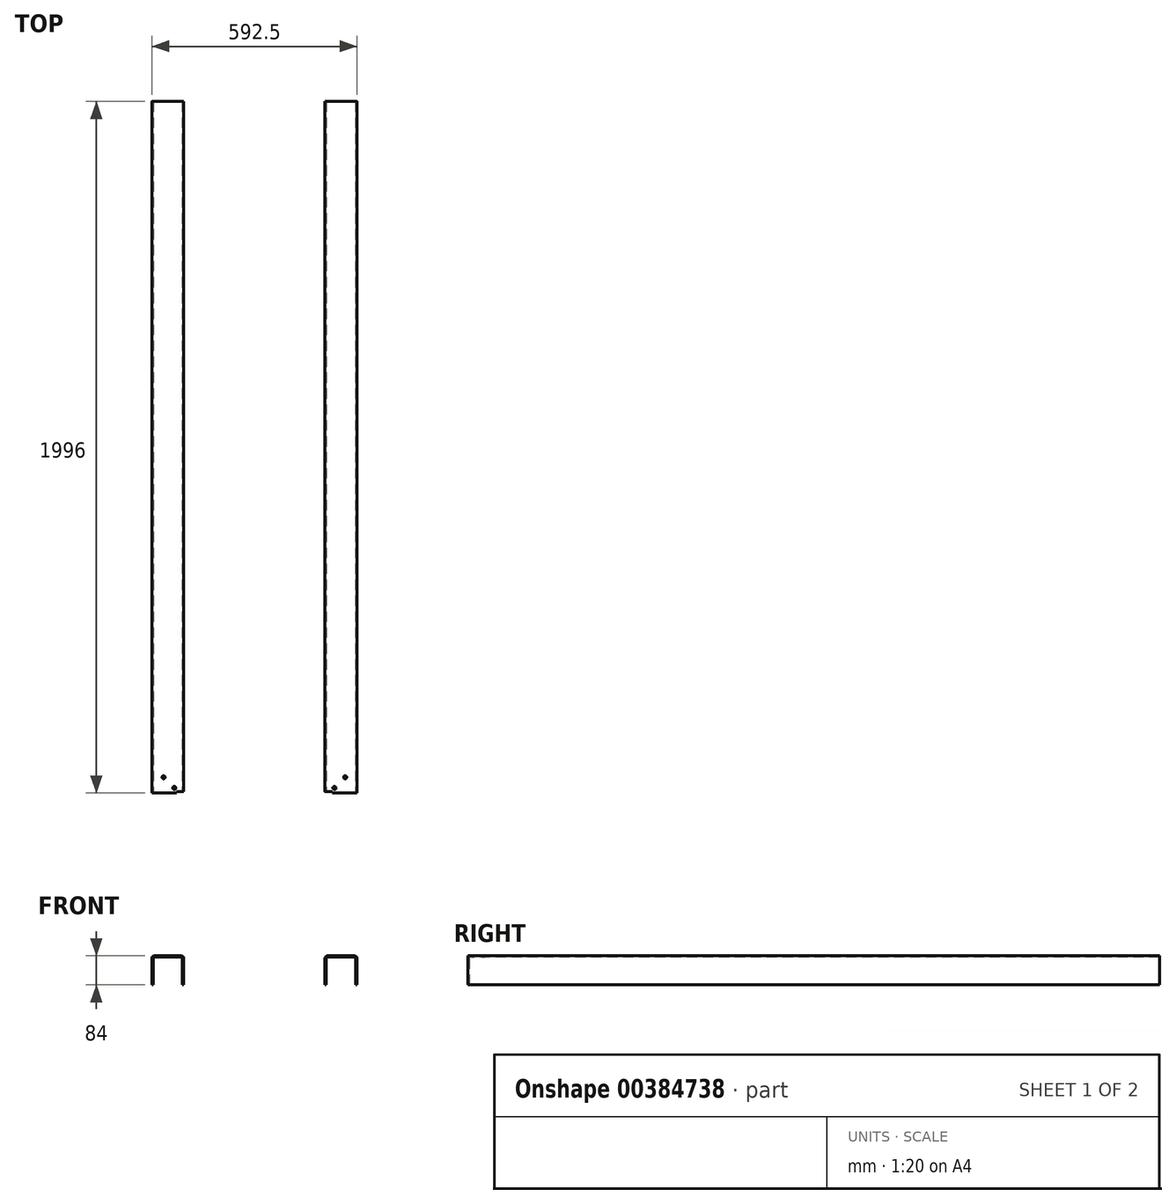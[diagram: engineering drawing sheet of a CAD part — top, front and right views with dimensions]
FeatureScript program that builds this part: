
annotation { "Feature Type Name" : "Feature", "Feature Type Description" : "" }
export const myFeature = defineFeature(function(context is Context, id is Id, definition is map)
    precondition{}
    {
        {
            var Q0;
            Q0=qCreatedBy(makeId("Front.planeOp"),FACE);
            var sketch = newSketch(context, id + "F0", { "sketchPlane" : qUnion([Q0])});
            skLineSegment(sketch, "E0.bottom", {"start": v(-46.25, -42) * mm, "end": v(-42.25, -42) * mm});
            skLineSegment(sketch, "E0.top", {"start": v(-38.25, 42) * mm, "end": v(38.25, 42) * mm});
            skLineSegment(sketch, "E0.left", {"start": v(-46.25, -42) * mm, "end": v(-46.25, 34) * mm});
            skLineSegment(sketch, "E0.right", {"start": v(46.25, -42) * mm, "end": v(46.25, 34) * mm});
            skPoint(sketch, "E0.middle", {"position": v(0, 0) * mm});
            skLineSegment(sketch, "E1", {"start": v(-42.25, -42) * mm, "end": v(-42.25, 34) * mm});
            skLineSegment(sketch, "E2", {"start": v(-38.25, 38) * mm, "end": v(38.25, 38) * mm});
            skLineSegment(sketch, "E3", {"start": v(42.25, 34) * mm, "end": v(42.25, -42) * mm});
            skLineSegment(sketch, "E4.trimOffspring", {"start": v(42.25, -42) * mm, "end": v(46.25, -42) * mm});
            skPoint(sketch, "E5.visualSharp", {"position": v(-42.25, 38) * mm});
            skArc(sketch, "E5.filletArc", {"start": v(-38.25, 38) * mm, "mid": v(-41.08, 36.83) * mm, "end": v(-42.25, 34) * mm});
            skPoint(sketch, "E6.visualSharp", {"position": v(42.25, 38) * mm});
            skArc(sketch, "E6.filletArc", {"start": v(42.25, 34) * mm, "mid": v(41.08, 36.83) * mm, "end": v(38.25, 38) * mm});
            skPoint(sketch, "E7.visualSharp", {"position": v(-46.25, 42) * mm});
            skArc(sketch, "E7.filletArc", {"start": v(-38.25, 42) * mm, "mid": v(-43.9, 39.66) * mm, "end": v(-46.25, 34) * mm});
            skPoint(sketch, "E8.visualSharp", {"position": v(46.25, 42) * mm});
            skArc(sketch, "E8.filletArc", {"start": v(46.25, 34) * mm, "mid": v(43.9, 39.66) * mm, "end": v(38.25, 42) * mm});
            skSolve(sketch);
        }
        {
            var Q0;
            Q0=makeQuery(id+"F0.imprint","IMPRINT",FACE,{"disambiguationData":[TD([[makeQuery(id+"F0.imprint","IMPRINT",EDGE,{"derivedFrom":sQuery(id+"F0.wireOp",EDGE,"E0.bottom")}),1.0]])]});
            extrude(context, id + "F1", {"entities" : qUnion([Q0]), "oppositeDirection" : true, "depth" : 1996 * mm});
        }
        {
            var Q0;
            Q0=qCreatedBy(makeId("Right.planeOp"),FACE);
            var Q1;
            Q1=makeQuery(id+"F1.opExtrude","CAP_EDGE",EDGE,{"disambiguationData":[OSD([sQuery(id+"F0.wireOp",EDGE,"E0.left")])],"isStart":true});
            cPlane(context, id + "F2", {"entities" : qUnion([Q0, Q1]), "cplaneType" : CPlaneType.LINE_ANGLE, "offset" : 25 * mm, "angle" : 0 * degree, "width" : 150 * mm, "height" : 150 * mm});
        }
        {
            var Q0;
            Q0=qCreatedBy(id+"F2.planeOp",FACE);
            var sketch = newSketch(context, id + "F3", { "sketchPlane" : qUnion([Q0])});
            skLineSegment(sketch, "E9.bottom", {"start": v(0, -43.13) * mm, "end": v(-4, -43.13) * mm});
            skLineSegment(sketch, "E9.top", {"start": v(0, 43.87) * mm, "end": v(-4, 43.87) * mm});
            skLineSegment(sketch, "E9.left", {"start": v(0, -43.13) * mm, "end": v(0, 43.87) * mm});
            skLineSegment(sketch, "E9.right", {"start": v(-4, -43.13) * mm, "end": v(-4, 43.87) * mm});
            skSolve(sketch);
        }
        {
            var Q0;
            Q0=makeQuery(id+"F3.imprint","IMPRINT",FACE,{"disambiguationData":[TD([[makeQuery(id+"F3.imprint","IMPRINT",EDGE,{"derivedFrom":sQuery(id+"F3.wireOp",EDGE,"E9.bottom")}),-1.0]])]});
            extrude(context, id + "F4", {"entities" : qUnion([Q0]), "operationType" : NewBodyOperationType.REMOVE, "oppositeDirection" : true, "depth" : 21.4 * mm});
        }
        {
            var Q0;
            Q0=makeQuery(id+"F1.opExtrude","SWEPT_FACE",FACE,{"disambiguationData":[OSD([sQuery(id+"F0.wireOp",EDGE,"E2")])]});
            var sketch = newSketch(context, id + "F5", { "sketchPlane" : qUnion([Q0])});
            skPoint(sketch, "E10.middle", {"position": v(0, 0) * mm});
            skLineSegment(sketch, "E11", {"start": v(18.92, 0) * mm, "end": v(-18.92, 0) * mm});
            skPoint(sketch, "E10.bottom.end.orphan", {"position": v(-18.92, 14.5) * mm});
            skPoint(sketch, "E10.bottom.start.orphan", {"position": v(18.92, 14.5) * mm});
            skCircle(sketch, "E12", {"center": v(-18.92, -14.5) * mm, "radius": 4.5 * mm});
            skPoint(sketch, "E10.left.end.orphan", {"position": v(18.92, -14.5) * mm});
            skSolve(sketch);
        }
        {
            var Q0;
            {var subQ6=sQuery(id+"F5.wireOp",EDGE,"E11");Q0=makeQuery(id+"F5.imprint","IMPRINT",FACE,{"disambiguationData":[TD([[makeQuery(id+"F5.imprint","IMPRINT",EDGE,{"derivedFrom":subQ6}),-1.0]])]});}
            var sketch = newSketch(context, id + "F6", { "sketchPlane" : qUnion([Q0])});
            skPoint(sketch, "E13.middle", {"position": v(0, 0) * mm});
            skCircle(sketch, "E14", {"center": v(12.06, -45.5) * mm, "radius": 4.5 * mm});
            skPoint(sketch, "E13.right.end.orphan", {"position": v(-12.06, -45.5) * mm});
            skPoint(sketch, "E13.bottom.end.orphan", {"position": v(-12.06, 45.5) * mm});
            skPoint(sketch, "E13.bottom.start.orphan", {"position": v(12.06, 45.5) * mm});
            skSolve(sketch);
        }
        {
            var Q0;
            Q0=makeQuery(id+"F6.imprint","IMPRINT",FACE,{"disambiguationData":[TD([[makeQuery(id+"F6.imprint","IMPRINT",EDGE,{"derivedFrom":sQuery(id+"F6.wireOp",EDGE,"E14")}),1.0]])]});
            var Q1;
            Q1=makeQuery(id+"F5.imprint","IMPRINT",FACE,{"disambiguationData":[TD([[makeQuery(id+"F5.imprint","IMPRINT",EDGE,{"derivedFrom":sQuery(id+"F5.wireOp",EDGE,"E12")}),1.0]])]});
            extrude(context, id + "F7", {"entities" : qUnion([Q0, Q1]), "operationType" : NewBodyOperationType.REMOVE, "oppositeDirection" : true, "depth" : 4 * mm});
        }
        {
            var Q0;
            Q0=qCreatedBy(makeId("Right.planeOp"),FACE);
            cPlane(context, id + "F8", {"entities" : qUnion([Q0]), "cplaneType" : CPlaneType.OFFSET, "offset" : 250 * mm, "oppositeDirection" : true, "width" : 150 * mm, "height" : 150 * mm});
        }
        {
            var Q0;
            Q0=makeQuery(id+"F1.opExtrude","SWEPT_BODY",BODY,{"disambiguationData":[OSD([sQuery(id+"F0.wireOp",EDGE,"E0.bottom"),sQuery(id+"F0.wireOp",EDGE,"E0.top"),sQuery(id+"F0.wireOp",EDGE,"E0.left"),sQuery(id+"F0.wireOp",EDGE,"E0.right"),sQuery(id+"F0.wireOp",EDGE,"E1"),sQuery(id+"F0.wireOp",EDGE,"E2"),sQuery(id+"F0.wireOp",EDGE,"E3"),sQuery(id+"F0.wireOp",EDGE,"E4.trimOffspring"),sQuery(id+"F0.wireOp",EDGE,"E5.filletArc"),sQuery(id+"F0.wireOp",EDGE,"E6.filletArc"),sQuery(id+"F0.wireOp",EDGE,"E7.filletArc"),sQuery(id+"F0.wireOp",EDGE,"E8.filletArc")])]});
            var Q1;
            Q1=qCreatedBy(id+"F8.planeOp",FACE);
            mirror(context, id + "F9", {"entities" : qUnion([Q0]), "mirrorPlane" : qUnion([Q1])});
        }
    });
